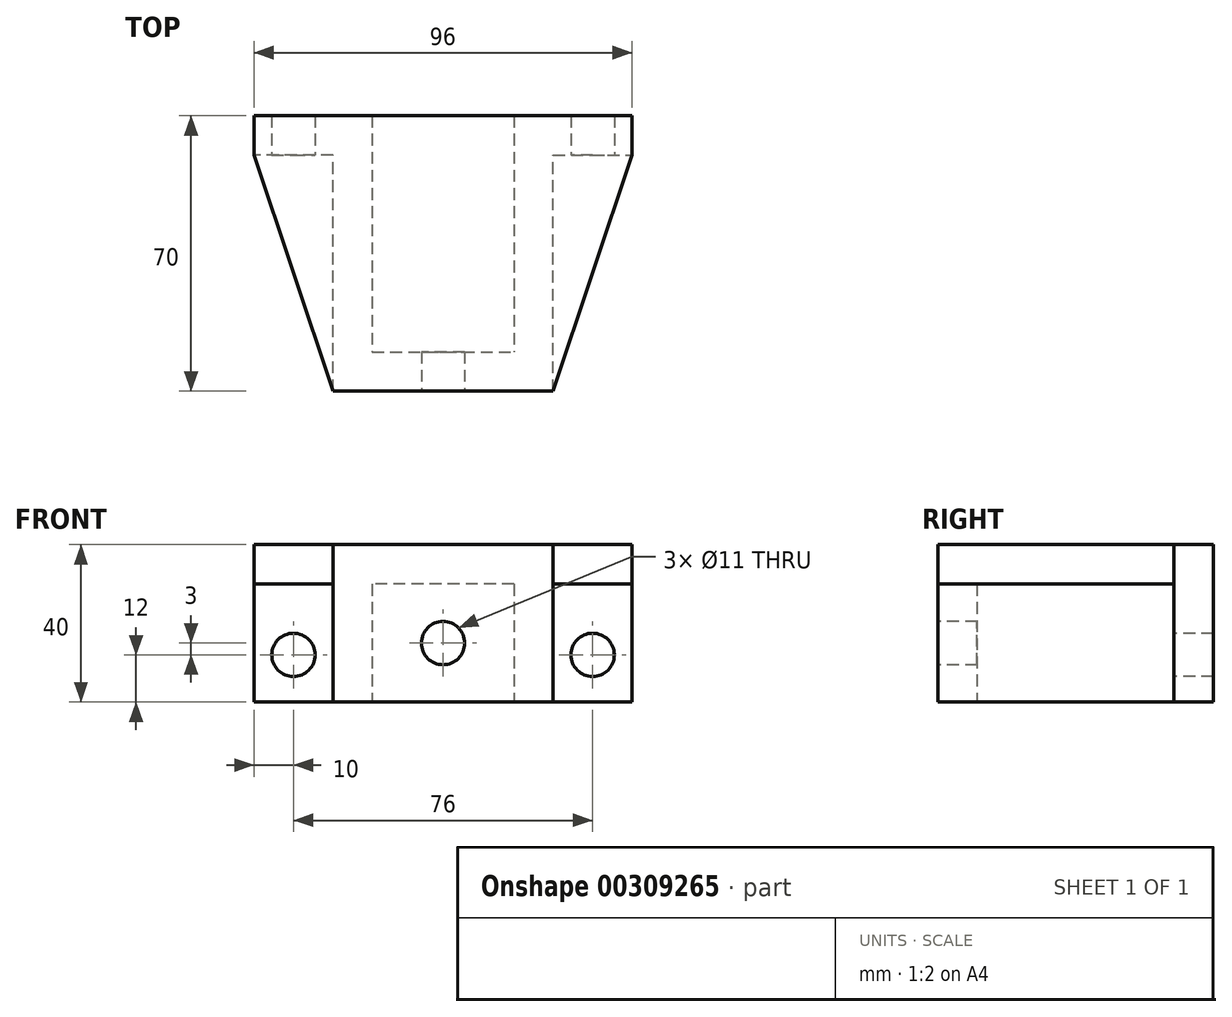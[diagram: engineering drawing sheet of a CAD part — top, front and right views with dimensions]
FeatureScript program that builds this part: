
annotation { "Feature Type Name" : "Feature", "Feature Type Description" : "" }
export const myFeature = defineFeature(function(context is Context, id is Id, definition is map)
    precondition{}
    {
        {
            var Q0;
            Q0=qCreatedBy(makeId("Front.planeOp"),FACE);
            var sketch = newSketch(context, id + "F0", { "sketchPlane" : qUnion([Q0])});
            skLineSegment(sketch, "E0.bottom", {"start": v(48, 20) * mm, "end": v(-48, 20) * mm});
            skLineSegment(sketch, "E0.top", {"start": v(48, -20) * mm, "end": v(-48, -20) * mm});
            skLineSegment(sketch, "E0.left", {"start": v(48, 20) * mm, "end": v(48, -20) * mm});
            skLineSegment(sketch, "E0.right", {"start": v(-48, 20) * mm, "end": v(-48, -20) * mm});
            skPoint(sketch, "E0.middle", {"position": v(0, 0) * mm});
            skSolve(sketch);
        }
        {
            var Q0;
            Q0=makeQuery(id+"F0.imprint","IMPRINT",FACE,{"disambiguationData":[TD([[makeQuery(id+"F0.imprint","IMPRINT",EDGE,{"derivedFrom":sQuery(id+"F0.wireOp",EDGE,"E0.bottom")}),1.0]])]});
            extrude(context, id + "F1", {"entities" : qUnion([Q0]), "depth" : 70 * mm});
        }
        {
            var Q0;
            Q0=makeQuery(id+"F1.opExtrude","CAP_FACE",FACE,{"disambiguationData":[OSD([sQuery(id+"F0.wireOp",EDGE,"E0.bottom"),sQuery(id+"F0.wireOp",EDGE,"E0.top"),sQuery(id+"F0.wireOp",EDGE,"E0.left"),sQuery(id+"F0.wireOp",EDGE,"E0.right")])],"isStart":false});
            var sketch = newSketch(context, id + "F2", { "sketchPlane" : qUnion([Q0])});
            skCircle(sketch, "E1", {"center": v(0, -5) * mm, "radius": 5.5 * mm});
            skCircle(sketch, "E2", {"center": v(38, -8) * mm, "radius": 5.5 * mm});
            skCircle(sketch, "E3", {"center": v(-38, -8) * mm, "radius": 5.5 * mm});
            skSolve(sketch);
        }
        {
            var Q0;
            Q0=makeQuery(id+"F2.imprint","IMPRINT",FACE,{"disambiguationData":[TD([[makeQuery(id+"F2.imprint","IMPRINT",EDGE,{"derivedFrom":sQuery(id+"F2.wireOp",EDGE,"E1")}),1.0]])]});
            extrude(context, id + "F3", {"entities" : qUnion([Q0]), "operationType" : NewBodyOperationType.REMOVE, "oppositeDirection" : true, "depth" : 10 * mm});
        }
        {
            var Q0;
            Q0=makeQuery(id+"F2.imprint","IMPRINT",FACE,{"disambiguationData":[TD([[makeQuery(id+"F2.imprint","IMPRINT",EDGE,{"derivedFrom":sQuery(id+"F2.wireOp",EDGE,"E3")}),1.0]])]});
            var Q1;
            Q1=makeQuery(id+"F2.imprint","IMPRINT",FACE,{"disambiguationData":[TD([[makeQuery(id+"F2.imprint","IMPRINT",EDGE,{"derivedFrom":sQuery(id+"F2.wireOp",EDGE,"E2")}),1.0]])]});
            extrude(context, id + "F4", {"entities" : qUnion([Q0, Q1]), "operationType" : NewBodyOperationType.REMOVE, "oppositeDirection" : true, "depth" : 80 * mm});
        }
        {
            var Q0;
            Q0=makeQuery(id+"F1.opExtrude","SWEPT_FACE",FACE,{"disambiguationData":[OSD([sQuery(id+"F0.wireOp",EDGE,"E0.top")])]});
            var sketch = newSketch(context, id + "F5", { "sketchPlane" : qUnion([Q0])});
            skLineSegment(sketch, "E4.bottom", {"start": v(-18, 0) * mm, "end": v(18, 0) * mm});
            skLineSegment(sketch, "E4.top", {"start": v(-18, 60) * mm, "end": v(18, 60) * mm});
            skLineSegment(sketch, "E4.left", {"start": v(-18, 0) * mm, "end": v(-18, 60) * mm});
            skLineSegment(sketch, "E4.right", {"start": v(18, 0) * mm, "end": v(18, 60) * mm});
            skSolve(sketch);
        }
        {
            var Q0;
            Q0=makeQuery(id+"F5.imprint","IMPRINT",FACE,{"disambiguationData":[TD([[makeQuery(id+"F5.imprint","IMPRINT",EDGE,{"derivedFrom":sQuery(id+"F5.wireOp",EDGE,"E4.bottom")}),-1.0]])]});
            extrude(context, id + "F6", {"entities" : qUnion([Q0]), "operationType" : NewBodyOperationType.REMOVE, "oppositeDirection" : true, "depth" : 30 * mm});
        }
        {
            var Q0;
            Q0=makeQuery(id+"F1.opExtrude","SWEPT_FACE",FACE,{"disambiguationData":[OSD([sQuery(id+"F0.wireOp",EDGE,"E0.top")])]});
            var sketch = newSketch(context, id + "F7", { "sketchPlane" : qUnion([Q0])});
            skLineSegment(sketch, "E5", {"start": v(28, 70) * mm, "end": v(48, 10) * mm});
            skLineSegment(sketch, "E6", {"start": v(28, 70) * mm, "end": v(28, 10) * mm});
            skLineSegment(sketch, "E7", {"start": v(28, 10) * mm, "end": v(48, 10) * mm});
            skLineSegment(sketch, "E8", {"start": v(-28, 70) * mm, "end": v(-28, 10) * mm});
            skLineSegment(sketch, "E9", {"start": v(-28, 10) * mm, "end": v(-48, 10) * mm});
            skLineSegment(sketch, "E10", {"start": v(-48, 10) * mm, "end": v(-28, 70) * mm});
            skSolve(sketch);
        }
        {
            var Q0;
            {var subQ0=sQuery(id+"F7.wireOp",EDGE,"E10");Q0=makeQuery(id+"F7.imprint","IMPRINT",FACE,{"disambiguationData":[TD([[makeQuery(id+"F7.imprint","IMPRINT",EDGE,{"derivedFrom":subQ0}),1.0]])]});}
            var Q1;
            {var subQ0=sQuery(id+"F7.wireOp",EDGE,"E5");Q1=makeQuery(id+"F7.imprint","IMPRINT",FACE,{"disambiguationData":[TD([[makeQuery(id+"F7.imprint","IMPRINT",EDGE,{"derivedFrom":subQ0}),1.0]])]});}
            extrude(context, id + "F8", {"entities" : qUnion([Q0, Q1]), "operationType" : NewBodyOperationType.REMOVE, "oppositeDirection" : true, "depth" : 45 * mm});
        }
        {
            var Q0;
            Q0 = qSketchRegion(id + "F7", true);
            extrude(context, id + "F9", {"entities" : qUnion([Q0]), "operationType" : NewBodyOperationType.REMOVE, "oppositeDirection" : true, "depth" : 30 * mm});
        }
    });
